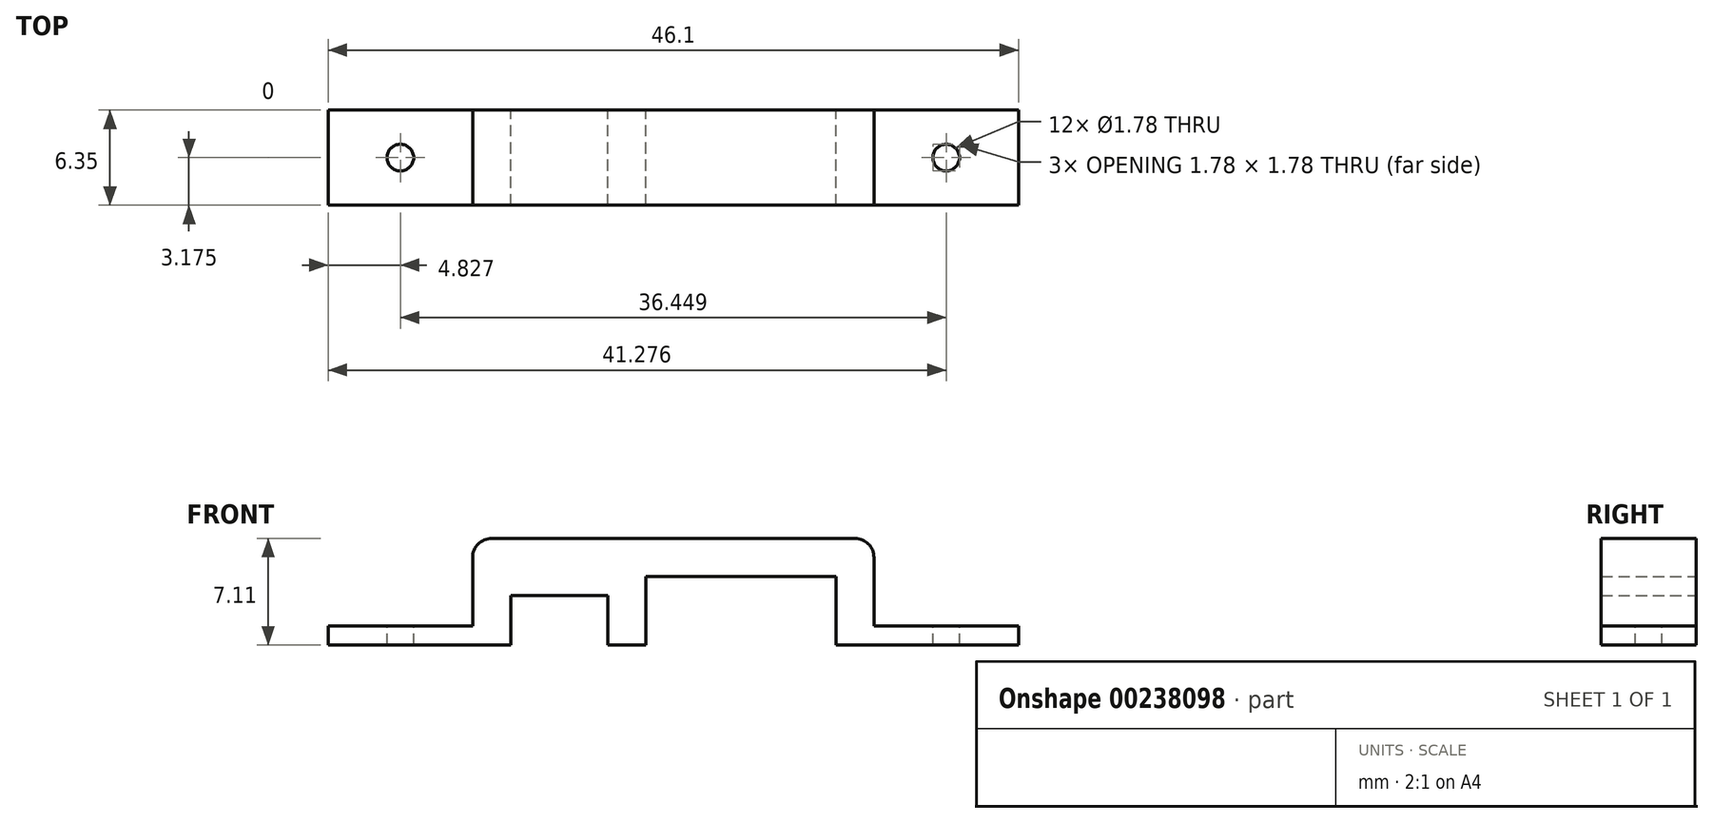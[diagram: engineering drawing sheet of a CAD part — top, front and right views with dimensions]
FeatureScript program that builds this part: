
annotation { "Feature Type Name" : "Feature", "Feature Type Description" : "" }
export const myFeature = defineFeature(function(context is Context, id is Id, definition is map)
    precondition{}
    {
        {
            var Q0;
            Q0=qCreatedBy(makeId("Front.planeOp"),FACE);
            var sketch = newSketch(context, id + "F0", { "sketchPlane" : qUnion([Q0])});
            skLineSegment(sketch, "E0", {"start": v(15.28, 0) * mm, "end": v(15.28, 4.57) * mm});
            skLineSegment(sketch, "E1", {"start": v(15.28, 4.57) * mm, "end": v(2.58, 4.57) * mm});
            skLineSegment(sketch, "E2", {"start": v(2.58, 4.57) * mm, "end": v(2.58, 0) * mm});
            skLineSegment(sketch, "E3", {"start": v(2.58, 0) * mm, "end": v(0.04, 0) * mm});
            skLineSegment(sketch, "E4", {"start": v(0.04, 0) * mm, "end": v(0.04, 3.3) * mm});
            skLineSegment(sketch, "E5", {"start": v(0.04, 3.3) * mm, "end": v(-6.44, 3.3) * mm});
            skLineSegment(sketch, "E6", {"start": v(-6.44, 3.3) * mm, "end": v(-6.44, 0) * mm});
            skLineSegment(sketch, "E7", {"start": v(-8.98, 1.27) * mm, "end": v(-8.98, 5.84) * mm});
            skLineSegment(sketch, "E8", {"start": v(-7.7, 7.11) * mm, "end": v(16.55, 7.11) * mm});
            skLineSegment(sketch, "E9", {"start": v(17.82, 5.84) * mm, "end": v(17.82, 1.27) * mm});
            skLineSegment(sketch, "E10", {"start": v(17.82, 0) * mm, "end": v(15.28, 0) * mm});
            skPoint(sketch, "E11.visualSharp", {"position": v(-8.98, 7.11) * mm});
            skArc(sketch, "E11.filletArc", {"start": v(-7.7, 7.11) * mm, "mid": v(-8.6, 6.74) * mm, "end": v(-8.98, 5.84) * mm});
            skPoint(sketch, "E12.visualSharp", {"position": v(17.82, 7.11) * mm});
            skArc(sketch, "E12.filletArc", {"start": v(17.82, 5.84) * mm, "mid": v(17.45, 6.74) * mm, "end": v(16.55, 7.11) * mm});
            skLineSegment(sketch, "E13", {"start": v(-8.98, 1.27) * mm, "end": v(-18.63, 1.27) * mm});
            skLineSegment(sketch, "E14", {"start": v(-18.63, 1.27) * mm, "end": v(-18.63, 0) * mm});
            skLineSegment(sketch, "E15", {"start": v(17.82, 1.27) * mm, "end": v(27.47, 1.27) * mm});
            skLineSegment(sketch, "E16", {"start": v(27.47, 1.27) * mm, "end": v(27.47, 0) * mm});
            skLineSegment(sketch, "E17", {"start": v(27.47, 0) * mm, "end": v(17.82, 0) * mm});
            skLineSegment(sketch, "E18", {"start": v(-18.63, 0) * mm, "end": v(-6.44, 0) * mm});
            skSolve(sketch);
        }
        {
            var Q0;
            Q0=makeQuery(id+"F0.imprint","IMPRINT",FACE,{"disambiguationData":[TD([[makeQuery(id+"F0.imprint","IMPRINT",EDGE,{"derivedFrom":sQuery(id+"F0.wireOp",EDGE,"E0")}),-1.0]])]});
            extrude(context, id + "F1", {"entities" : qUnion([Q0]), "depth" : 6.35 * mm});
        }
        {
            var Q0;
            Q0=makeQuery(id+"F1.opExtrude","SWEPT_FACE",FACE,{"disambiguationData":[OSD([sQuery(id+"F0.wireOp",EDGE,"E13")])]});
            var sketch = newSketch(context, id + "F2", { "sketchPlane" : qUnion([Q0])});
            skCircle(sketch, "E19", {"center": v(-13.8, -3.18) * mm, "radius": 0.89 * mm});
            skPoint(sketch, "E19.centerSnap0", {"position": v(-13.8, 0) * mm});
            skCircle(sketch, "E20", {"center": v(22.65, -3.18) * mm, "radius": 0.89 * mm});
            skSolve(sketch);
        }
        {
            var Q0;
            Q0=makeQuery(id+"F2.imprint","IMPRINT",FACE,{"disambiguationData":[TD([[makeQuery(id+"F2.imprint","IMPRINT",EDGE,{"derivedFrom":sQuery(id+"F2.wireOp",EDGE,"E19")}),1.0]])]});
            var Q1;
            Q1=makeQuery(id+"F2.imprint","IMPRINT",FACE,{"disambiguationData":[TD([[makeQuery(id+"F2.imprint","IMPRINT",EDGE,{"derivedFrom":sQuery(id+"F2.wireOp",EDGE,"E20")}),1.0]])]});
            extrude(context, id + "F3", {"entities" : qUnion([Q0, Q1]), "operationType" : NewBodyOperationType.REMOVE, "endBound" : BoundingType.UP_TO_NEXT, "oppositeDirection" : true, "depth" : 25.4 * mm});
        }
    });
